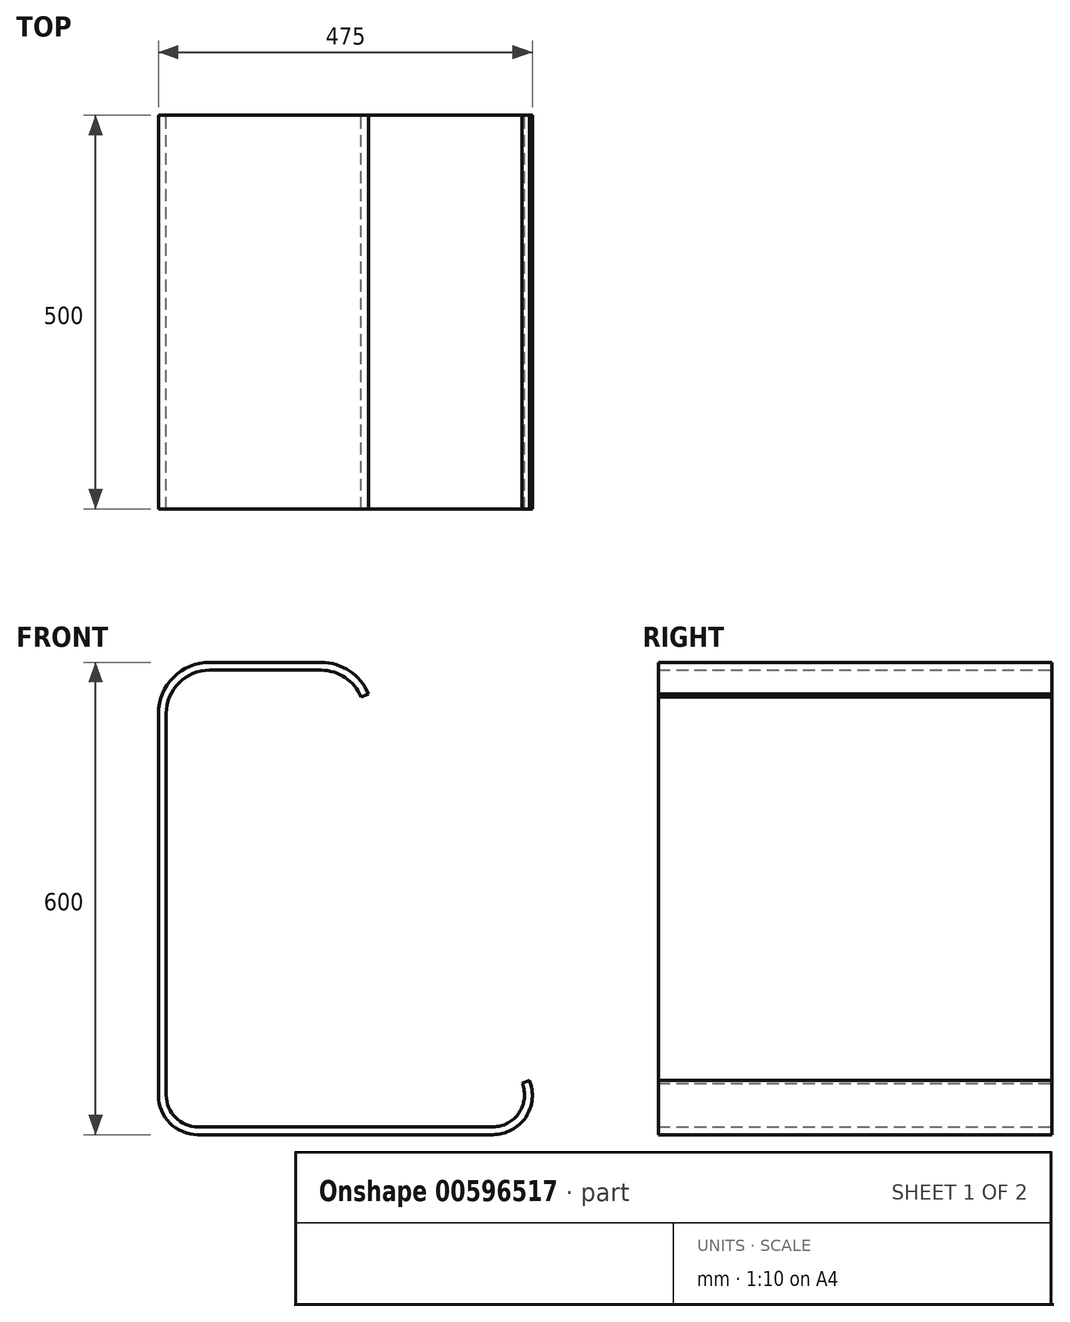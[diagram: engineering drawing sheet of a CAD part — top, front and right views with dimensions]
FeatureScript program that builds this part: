
annotation { "Feature Type Name" : "Feature", "Feature Type Description" : "" }
export const myFeature = defineFeature(function(context is Context, id is Id, definition is map)
    precondition{}
    {
        {
            var Q0;
            Q0=qCreatedBy(makeId("Front.planeOp"),FACE);
            var sketch = newSketch(context, id + "F0", { "sketchPlane" : qUnion([Q0])});
            skLineSegment(sketch, "E0.bottom", {"start": v(-250, 300) * mm, "end": v(0, 300) * mm});
            skLineSegment(sketch, "E0.top", {"start": v(-200, -300) * mm, "end": v(175, -300) * mm});
            skLineSegment(sketch, "E0.left", {"start": v(-250, 235) * mm, "end": v(-250, -250) * mm});
            skPoint(sketch, "E0.middle", {"position": v(0, 0) * mm});
            skLineSegment(sketch, "E1", {"start": v(-185, 300) * mm, "end": v(-43.33, 300) * mm});
            skLineSegment(sketch, "E2", {"start": v(16.67, 260) * mm, "end": v(221.15, -230.77) * mm});
            skPoint(sketch, "E0.right.start.orphan", {"position": v(250, 300) * mm});
            skPoint(sketch, "E3.visualSharp", {"position": v(-250, 300) * mm});
            skArc(sketch, "E3.filletArc", {"start": v(-185, 300) * mm, "mid": v(-230.96, 280.96) * mm, "end": v(-250, 235) * mm});
            skPoint(sketch, "E4.visualSharp", {"position": v(0, 300) * mm});
            skArc(sketch, "E4.filletArc", {"start": v(16.67, 260) * mm, "mid": v(-7.28, 289.08) * mm, "end": v(-43.33, 300) * mm});
            skPoint(sketch, "E5.visualSharp", {"position": v(-250, -300) * mm});
            skArc(sketch, "E5.filletArc", {"start": v(-250, -250) * mm, "mid": v(-235.36, -285.36) * mm, "end": v(-200, -300) * mm});
            skPoint(sketch, "E6.visualSharp", {"position": v(250, -300) * mm});
            skArc(sketch, "E6.filletArc", {"start": v(175, -300) * mm, "mid": v(216.6, -277.74) * mm, "end": v(221.15, -230.77) * mm});
            skArc(sketch, "E7.0", {"start": v(-185, 290) * mm, "mid": v(-223.9, 273.9) * mm, "end": v(-240, 235) * mm});
            skLineSegment(sketch, "E7.1", {"start": v(-185, 290) * mm, "end": v(-43.33, 290) * mm});
            skLineSegment(sketch, "E7.2", {"start": v(-240, 235) * mm, "end": v(-240, -250) * mm});
            skArc(sketch, "E7.3", {"start": v(7.44, 256.15) * mm, "mid": v(-12.82, 280.76) * mm, "end": v(-43.33, 290) * mm});
            skArc(sketch, "E7.4", {"start": v(-240, -250) * mm, "mid": v(-228.28, -278.28) * mm, "end": v(-200, -290) * mm});
            skLineSegment(sketch, "E7.5", {"start": v(-200, -290) * mm, "end": v(175, -290) * mm});
            skArc(sketch, "E7.6", {"start": v(175, -290) * mm, "mid": v(208.28, -272.19) * mm, "end": v(211.92, -234.62) * mm});
            skLineSegment(sketch, "E7.7", {"start": v(7.44, 256.15) * mm, "end": v(211.92, -234.62) * mm});
            skSolve(sketch);
        }
        {
            var Q0;
            Q0=makeQuery(id+"F0.imprint","IMPRINT",FACE,{"disambiguationData":[TD([[makeQuery(id+"F0.imprint","IMPRINT",EDGE,{"derivedFrom":sQuery(id+"F0.wireOp",EDGE,"E0.top")}),1.0]])]});
            extrude(context, id + "F1", {"entities" : qUnion([Q0]), "depth" : 500 * mm, "offsetDistance" : 25 * mm});
        }
        {
            var Q0;
            Q0=makeQuery(id+"F1.opExtrude","SWEPT_FACE",FACE,{"disambiguationData":[OSD([sQuery(id+"F0.wireOp",EDGE,"E2")])]});
            var sketch = newSketch(context, id + "F2", { "sketchPlane" : qUnion([Q0])});
            skSolve(sketch);
        }
        {
            var Q0;
            Q0 = qSketchRegion(id + "F2", true);
            var Q1;
            {var subQ0=sQuery(id+"F0.wireOp",EDGE,"E2");Q1=makeQuery(id+"F2.imprint","IMPRINT",FACE,{"disambiguationData":[TD([[makeQuery(id+"F2.imprint","IMPRINT",EDGE,{"derivedFrom":makeQuery(id+"F1.opExtrude","CAP_EDGE",EDGE,{"disambiguationData":[OSD([subQ0])],"isStart":true})}),-1.0]])]});}
            extrude(context, id + "F3", {"entities" : qUnion([Q0, Q1]), "operationType" : NewBodyOperationType.REMOVE, "oppositeDirection" : true, "depth" : 25 * mm, "offsetDistance" : 25 * mm});
        }
    });
